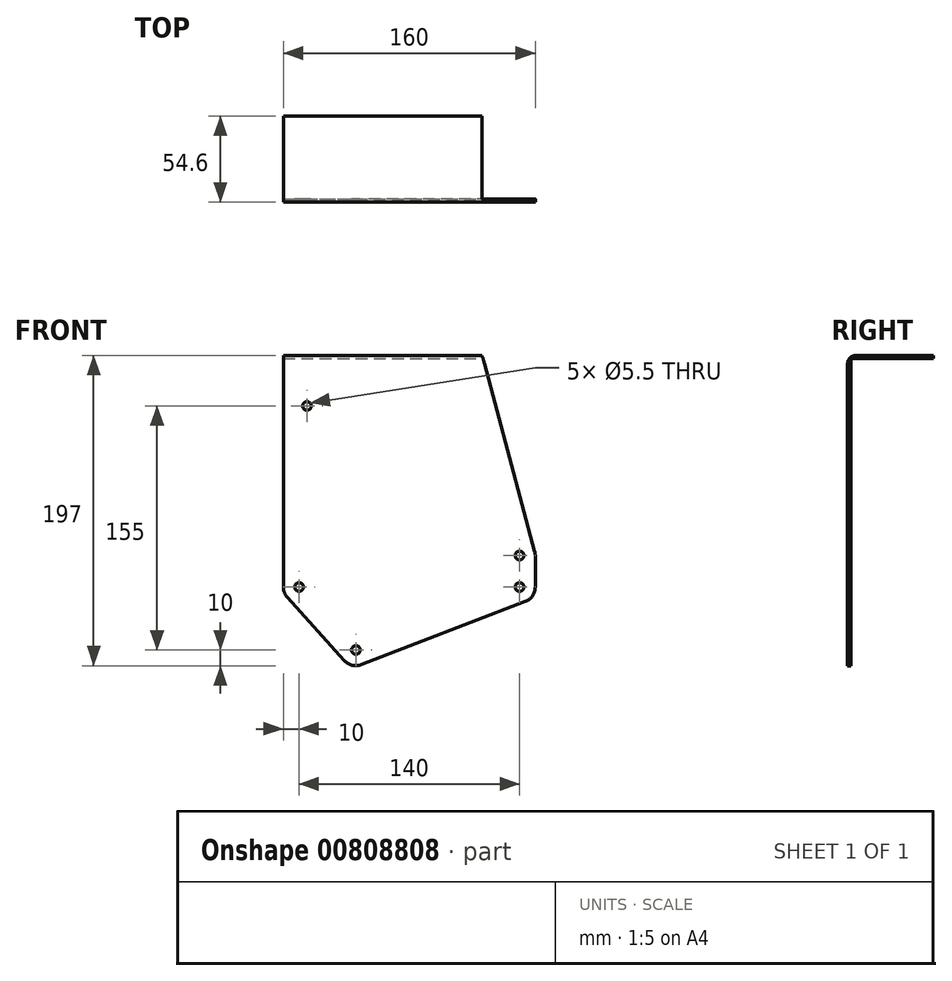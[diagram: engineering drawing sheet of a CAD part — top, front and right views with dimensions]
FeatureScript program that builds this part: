
annotation { "Feature Type Name" : "Feature", "Feature Type Description" : "" }
export const myFeature = defineFeature(function(context is Context, id is Id, definition is map)
    precondition{}
    {
        {
            var Q0;
            Q0=qCreatedBy(makeId("Front.planeOp"),FACE);
            cPlane(context, id + "F0", {"entities" : qUnion([Q0]), "cplaneType" : CPlaneType.OFFSET, "offset" : 35 * mm, "width" : 150 * mm, "height" : 150 * mm});
        }
        {
            var Q0;
            Q0=qCreatedBy(id+"F0.planeOp",FACE);
            var sketch = newSketch(context, id + "F1", { "sketchPlane" : qUnion([Q0])});
            skCircle(sketch, "E0", {"center": v(-103.92, -60) * mm, "radius": 2.75 * mm});
            skLineSegment(sketch, "E1", {"start": v(-103.92, -60) * mm, "end": v(-101.54, -58.63) * mm});
            skCircle(sketch, "E2", {"center": v(0, 0) * mm, "radius": 2.75 * mm});
            skLineSegment(sketch, "E3", {"start": v(-23.68, 127) * mm, "end": v(-150, 127) * mm});
            skArc(sketch, "E4", {"start": v(10, 0) * mm, "mid": v(9.91, 1.3) * mm, "end": v(9.66, 2.59) * mm});
            skLineSegment(sketch, "E5", {"start": v(9.66, 2.59) * mm, "end": v(-23.68, 127) * mm});
            skArc(sketch, "E6", {"start": v(-111.35, -66.7) * mm, "mid": v(-105.48, -69.88) * mm, "end": v(-98.92, -68.66) * mm});
            skLineSegment(sketch, "E7.trimOffspring", {"start": v(-2.38, -1.37) * mm, "end": v(0, 0) * mm});
            skCircle(sketch, "E8", {"center": v(-140, -20) * mm, "radius": 2.75 * mm});
            skArc(sketch, "E9", {"start": v(-150, -20) * mm, "mid": v(-149.33, -23.59) * mm, "end": v(-147.43, -26.7) * mm});
            skCircle(sketch, "E10", {"center": v(0, -20) * mm, "radius": 2.75 * mm});
            skCircle(sketch, "E11", {"center": v(-135, 95) * mm, "radius": 2.75 * mm});
            skLineSegment(sketch, "E12", {"start": v(-150, 127) * mm, "end": v(-150, -20) * mm});
            skLineSegment(sketch, "E13", {"start": v(-147.43, -26.7) * mm, "end": v(-111.35, -66.7) * mm});
            skArc(sketch, "E14", {"start": v(3.6, -29.33) * mm, "mid": v(8.24, -25.66) * mm, "end": v(10, -20) * mm});
            skLineSegment(sketch, "E15", {"start": v(3.6, -29.33) * mm, "end": v(-100.33, -69.33) * mm});
            skLineSegment(sketch, "E16", {"start": v(10, 0) * mm, "end": v(10, -20) * mm});
            skSolve(sketch);
        }
        {
            var Q0;
            Q0=makeQuery(id+"F1.imprint","IMPRINT",FACE,{"disambiguationData":[TD([[makeQuery(id+"F1.imprint","IMPRINT",EDGE,{"derivedFrom":sQuery(id+"F1.wireOp",EDGE,"E0")}),-1.0]])]});
            extrude(context, id + "F2", {"entities" : qUnion([Q0]), "depth" : 2 * mm, "offsetDistance" : 25 * mm});
        }
        {
            var Q0;
            Q0=makeQuery(id+"F2.opExtrude","CAP_FACE",FACE,{"disambiguationData":[OSD([sQuery(id+"F1.wireOp",EDGE,"E0"),sQuery(id+"F1.wireOp",EDGE,"E2"),sQuery(id+"F1.wireOp",EDGE,"E3"),sQuery(id+"F1.wireOp",EDGE,"E4"),sQuery(id+"F1.wireOp",EDGE,"E5"),sQuery(id+"F1.wireOp",EDGE,"E6"),sQuery(id+"F1.wireOp",EDGE,"E8"),sQuery(id+"F1.wireOp",EDGE,"E9"),sQuery(id+"F1.wireOp",EDGE,"E10"),sQuery(id+"F1.wireOp",EDGE,"E11"),sQuery(id+"F1.wireOp",EDGE,"E12"),sQuery(id+"F1.wireOp",EDGE,"E13"),sQuery(id+"F1.wireOp",EDGE,"E14"),sQuery(id+"F1.wireOp",EDGE,"E15"),sQuery(id+"F1.wireOp",EDGE,"E16")])],"isStart":true});
            var sketch = newSketch(context, id + "F3", { "sketchPlane" : qUnion([Q0])});
            skLineSegment(sketch, "E17.bottom", {"start": v(150, 127) * mm, "end": v(23.68, 127) * mm});
            skLineSegment(sketch, "E17.top", {"start": v(150, 125) * mm, "end": v(23.68, 125) * mm});
            skLineSegment(sketch, "E17.left", {"start": v(150, 127) * mm, "end": v(150, 125) * mm});
            skLineSegment(sketch, "E17.right", {"start": v(23.68, 127) * mm, "end": v(23.68, 125) * mm});
            skSolve(sketch);
        }
        {
            var Q0;
            Q0 = qSketchRegion(id + "F3", true);
            extrude(context, id + "F4", {"entities" : qUnion([Q0]), "operationType" : NewBodyOperationType.ADD, "depth" : 35 * mm, "offsetDistance" : 25 * mm});
        }
        {
            var Q0;
            Q0=makeQuery(id+"F2.opExtrude","CAP_EDGE",EDGE,{"disambiguationData":[OSD([sQuery(id+"F1.wireOp",EDGE,"E3")])],"isStart":false});
            var Q1;
            Q1=makeQuery(id+"F4.opExtrude","CAP_EDGE",EDGE,{"disambiguationData":[OSD([sQuery(id+"F3.wireOp",EDGE,"E17.top")])],"isStart":true});
            fillet(context, id + "F5", {"entities" : qUnion([Q0, Q1]), "radius" : 5 * mm, "tangentPropagation" : true, "allowEdgeOverflow" : false});
        }
        {
            var Q0;
            Q0=makeQuery(id+"F4.opExtrude","CAP_FACE",FACE,{"disambiguationData":[OSD([sQuery(id+"F3.wireOp",EDGE,"E17.bottom"),sQuery(id+"F3.wireOp",EDGE,"E17.top"),sQuery(id+"F3.wireOp",EDGE,"E17.left"),sQuery(id+"F3.wireOp",EDGE,"E17.right")])],"isStart":false});
            extrude(context, id + "F6", {"entities" : qUnion([Q0]), "operationType" : NewBodyOperationType.ADD, "depth" : 17.6 * mm, "offsetDistance" : 25 * mm});
        }
    });
